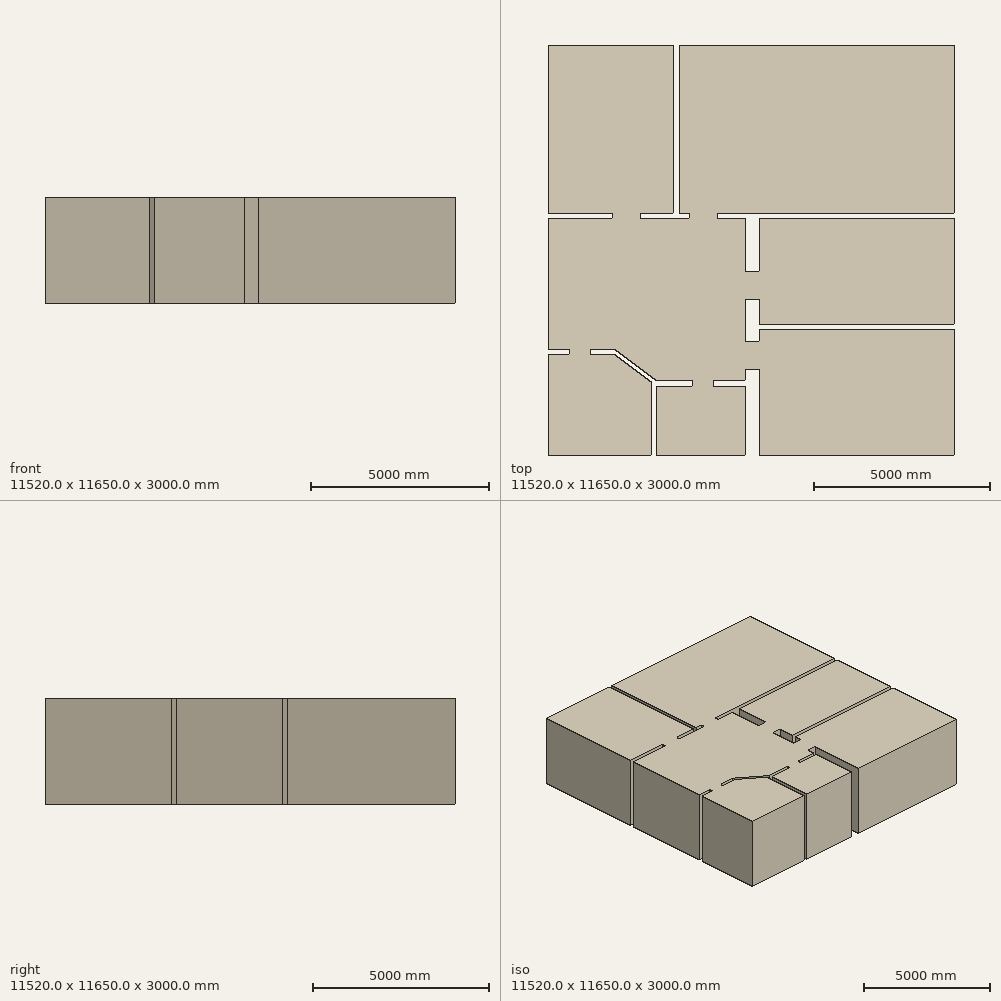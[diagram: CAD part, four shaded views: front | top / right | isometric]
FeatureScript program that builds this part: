
annotation { "Feature Type Name" : "Feature", "Feature Type Description" : "" }
export const myFeature = defineFeature(function(context is Context, id is Id, definition is map)
    precondition{}
    {
        {
            var Q0;
            Q0=qCreatedBy(makeId("Top.planeOp"),FACE);
            var sketch = newSketch(context, id + "F0", { "sketchPlane" : qUnion([Q0])});
            skLineSegment(sketch, "E0", {"start": v(0, 0) * mm, "end": v(-7820, 0) * mm});
            skLineSegment(sketch, "E1", {"start": v(-7820, 0) * mm, "end": v(-7820, -4760) * mm});
            skLineSegment(sketch, "E2", {"start": v(-7970, -4760) * mm, "end": v(-7970, 0) * mm});
            skLineSegment(sketch, "E3", {"start": v(-7970, 0) * mm, "end": v(-11520, 0) * mm});
            skLineSegment(sketch, "E4", {"start": v(-11520, 0) * mm, "end": v(-11520, -4760) * mm});
            skLineSegment(sketch, "E5", {"start": v(-11520, -11650) * mm, "end": v(-8610, -11650) * mm});
            skLineSegment(sketch, "E6", {"start": v(-8610, -11650) * mm, "end": v(-8610, -9560) * mm});
            skLineSegment(sketch, "E7", {"start": v(-8610, -9560) * mm, "end": v(-9636.67, -8790) * mm});
            skLineSegment(sketch, "E8", {"start": v(-8450, -9530) * mm, "end": v(-7440, -9530) * mm});
            skLineSegment(sketch, "E9", {"start": v(-8450, -11650) * mm, "end": v(-8450, -9680) * mm});
            skLineSegment(sketch, "E10", {"start": v(-8450, -9680) * mm, "end": v(-7440, -9680) * mm});
            skLineSegment(sketch, "E11", {"start": v(-11520, -4760) * mm, "end": v(-9720, -4760) * mm});
            skLineSegment(sketch, "E12", {"start": v(-9720, -4760) * mm, "end": v(-9720, -4910) * mm});
            skLineSegment(sketch, "E13", {"start": v(-9720, -4910) * mm, "end": v(-11520, -4910) * mm});
            skLineSegment(sketch, "E14", {"start": v(-7970, -4760) * mm, "end": v(-8920, -4760) * mm});
            skLineSegment(sketch, "E15", {"start": v(-8920, -4760) * mm, "end": v(-8920, -4910) * mm});
            skLineSegment(sketch, "E16", {"start": v(-8920, -4910) * mm, "end": v(-7519.39, -4910) * mm});
            skLineSegment(sketch, "E17", {"start": v(-7519.39, -4760) * mm, "end": v(-7820, -4760) * mm});
            skLineSegment(sketch, "E18", {"start": v(-9636.67, -8790) * mm, "end": v(-10336.67, -8790) * mm});
            skLineSegment(sketch, "E19", {"start": v(-11520, -11650) * mm, "end": v(-11520, -8790) * mm});
            skLineSegment(sketch, "E20", {"start": v(-11520, -8640) * mm, "end": v(-11520, -4910) * mm});
            skLineSegment(sketch, "E21", {"start": v(-10936.67, -8640) * mm, "end": v(-10936.67, -8790) * mm});
            skLineSegment(sketch, "E22", {"start": v(-10336.67, -8640) * mm, "end": v(-10336.67, -8790) * mm});
            skLineSegment(sketch, "E23", {"start": v(-11520, -8640) * mm, "end": v(-10936.67, -8640) * mm});
            skLineSegment(sketch, "E24.trimOffspring", {"start": v(-10936.67, -8790) * mm, "end": v(-11520, -8790) * mm});
            skLineSegment(sketch, "E25", {"start": v(0, 0) * mm, "end": v(0, -4760) * mm});
            skLineSegment(sketch, "E26", {"start": v(0, -4910) * mm, "end": v(0, -7930) * mm});
            skLineSegment(sketch, "E27", {"start": v(0, -11650) * mm, "end": v(-5530, -11650) * mm});
            skLineSegment(sketch, "E28", {"start": v(-5940, -11650) * mm, "end": v(-5940, -9680) * mm});
            skLineSegment(sketch, "E29", {"start": v(-5530, -4760) * mm, "end": v(-5940, -4760) * mm});
            skLineSegment(sketch, "E30", {"start": v(-5940, -4910) * mm, "end": v(-5940, -6420) * mm});
            skLineSegment(sketch, "E31", {"start": v(-8450, -11650) * mm, "end": v(-5940, -11650) * mm});
            skLineSegment(sketch, "E32", {"start": v(-7519.39, -4760) * mm, "end": v(-7519.39, -4910) * mm});
            skLineSegment(sketch, "E33", {"start": v(-6719.39, -4760) * mm, "end": v(-6719.39, -4910) * mm});
            skLineSegment(sketch, "E34", {"start": v(-5940, -4910) * mm, "end": v(-6719.39, -4910) * mm});
            skLineSegment(sketch, "E35", {"start": v(-6719.39, -4760) * mm, "end": v(-5940, -4760) * mm});
            skLineSegment(sketch, "E36", {"start": v(0, -4760) * mm, "end": v(-5530, -4760) * mm});
            skLineSegment(sketch, "E37", {"start": v(0, -7930) * mm, "end": v(-5530, -7930) * mm});
            skLineSegment(sketch, "E38", {"start": v(-10336.67, -8640) * mm, "end": v(-9636.67, -8640) * mm});
            skLineSegment(sketch, "E39", {"start": v(-9636.67, -8640) * mm, "end": v(-8450, -9530) * mm});
            skLineSegment(sketch, "E40", {"start": v(-5530, -4910) * mm, "end": v(0, -4910) * mm});
            skLineSegment(sketch, "E41.trimOffspring", {"start": v(-5530, -7930) * mm, "end": v(-5530, -7220) * mm});
            skLineSegment(sketch, "E42", {"start": v(-5530, -11650) * mm, "end": v(-5530, -9197.85) * mm});
            skLineSegment(sketch, "E43", {"start": v(-5530, -8080) * mm, "end": v(0, -8080) * mm});
            skLineSegment(sketch, "E44", {"start": v(0, -8080) * mm, "end": v(0, -11650) * mm});
            skLineSegment(sketch, "E45", {"start": v(-5940, -6420) * mm, "end": v(-5530, -6420) * mm});
            skLineSegment(sketch, "E46", {"start": v(-5940, -7220) * mm, "end": v(-5530, -7220) * mm});
            skLineSegment(sketch, "E47.trimOffspring", {"start": v(-5530, -6420) * mm, "end": v(-5530, -4910) * mm});
            skLineSegment(sketch, "E48.trimOffspring", {"start": v(-5940, -7220) * mm, "end": v(-5940, -8397.85) * mm});
            skLineSegment(sketch, "E49", {"start": v(-5940, -8397.85) * mm, "end": v(-5530, -8397.85) * mm});
            skLineSegment(sketch, "E50", {"start": v(-5530, -9197.85) * mm, "end": v(-5940, -9197.85) * mm});
            skLineSegment(sketch, "E51.trimOffspring", {"start": v(-5530, -8397.85) * mm, "end": v(-5530, -8080) * mm});
            skLineSegment(sketch, "E52.trimOffspring", {"start": v(-5940, -9197.85) * mm, "end": v(-5940, -9530) * mm});
            skLineSegment(sketch, "E53", {"start": v(-7440, -9530) * mm, "end": v(-7440, -9680) * mm});
            skLineSegment(sketch, "E54", {"start": v(-6840, -9530) * mm, "end": v(-6840, -9680) * mm});
            skLineSegment(sketch, "E55.trimOffspring", {"start": v(-6840, -9530) * mm, "end": v(-5940, -9530) * mm});
            skLineSegment(sketch, "E56.trimOffspring", {"start": v(-6840, -9680) * mm, "end": v(-5940, -9680) * mm});
            skSolve(sketch);
        }
        {
            var Q0;
            Q0 = qSketchRegion(id + "F0", true);
            extrude(context, id + "F1", {"entities" : qUnion([Q0]), "oppositeDirection" : true, "depth" : 3000 * mm});
        }
    });
